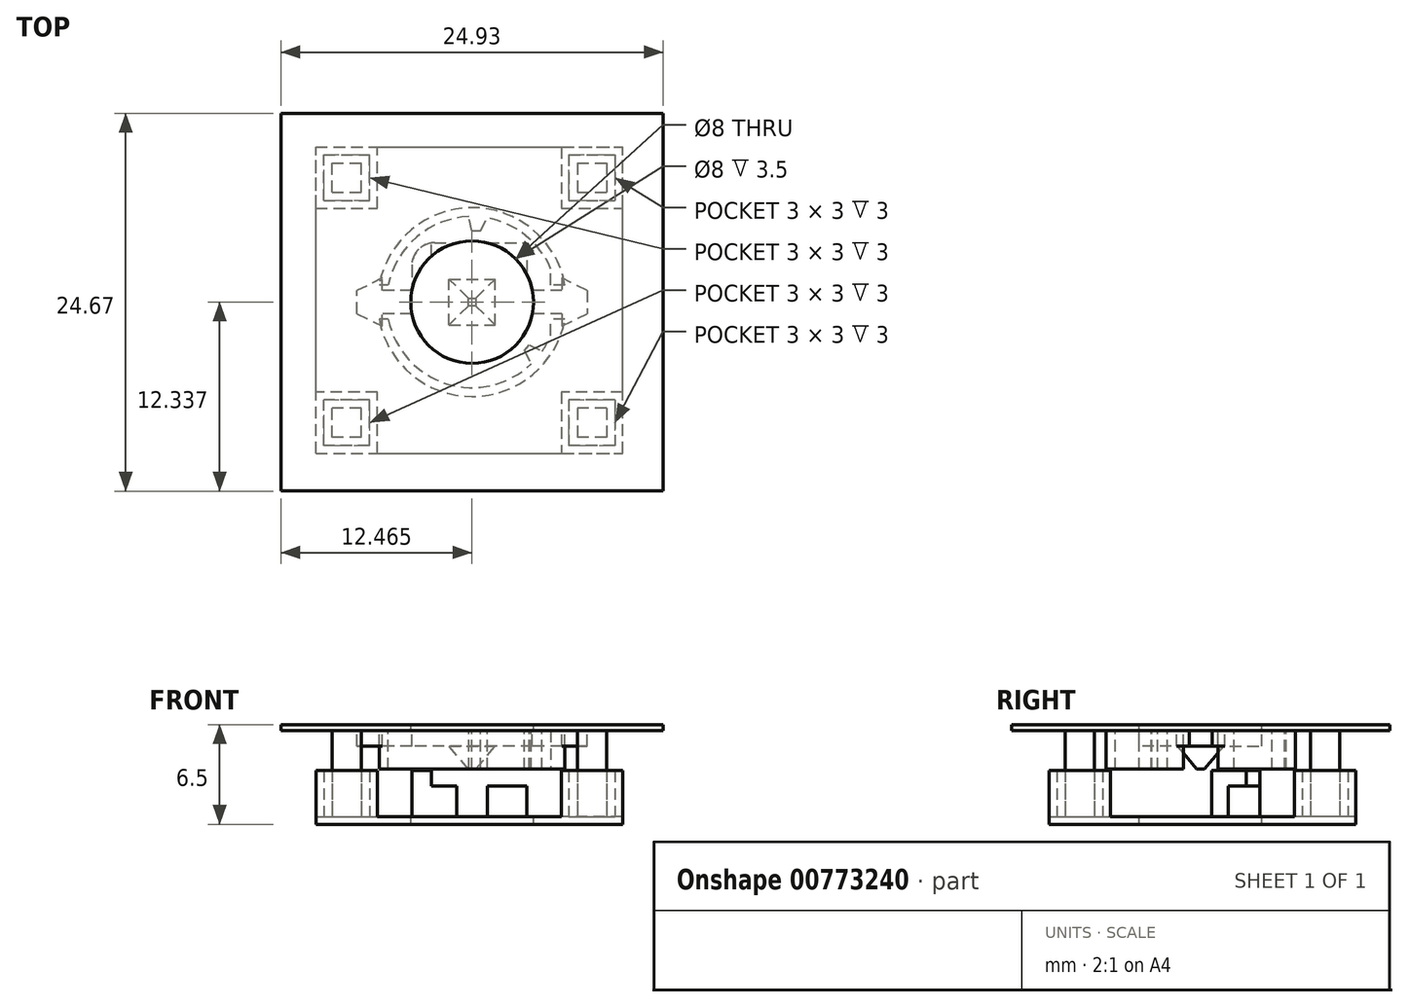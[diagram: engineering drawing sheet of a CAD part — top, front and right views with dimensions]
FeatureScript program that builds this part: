
annotation { "Feature Type Name" : "Feature", "Feature Type Description" : "" }
export const myFeature = defineFeature(function(context is Context, id is Id, definition is map)
    precondition{}
    {
        {
            var Q0;
            Q0=qCreatedBy(makeId("Top.planeOp"),FACE);
            var sketch = newSketch(context, id + "F0", { "sketchPlane" : qUnion([Q0])});
            skLineSegment(sketch, "E0.bottom", {"start": v(0, 0) * mm, "end": v(20, 0) * mm});
            skLineSegment(sketch, "E0.top", {"start": v(0, 20) * mm, "end": v(20, 20) * mm});
            skLineSegment(sketch, "E0.left", {"start": v(0, 0) * mm, "end": v(0, 20) * mm});
            skLineSegment(sketch, "E0.right", {"start": v(20, 0) * mm, "end": v(20, 20) * mm});
            skSolve(sketch);
        }
        {
            var Q0;
            Q0=makeQuery(id+"F0.imprint","IMPRINT",FACE,{"disambiguationData":[TD([[makeQuery(id+"F0.imprint","IMPRINT",EDGE,{"derivedFrom":sQuery(id+"F0.wireOp",EDGE,"E0.bottom")}),1.0]])]});
            extrude(context, id + "F1", {"entities" : qUnion([Q0]), "depth" : 0.5 * mm, "offsetDistance" : 25 * mm});
        }
        {
            var Q0;
            Q0=makeQuery(id+"F1.opExtrude","CAP_FACE",FACE,{"disambiguationData":[OSD([sQuery(id+"F0.wireOp",EDGE,"E0.bottom"),sQuery(id+"F0.wireOp",EDGE,"E0.top"),sQuery(id+"F0.wireOp",EDGE,"E0.left"),sQuery(id+"F0.wireOp",EDGE,"E0.right")])],"isStart":false});
            var sketch = newSketch(context, id + "F2", { "sketchPlane" : qUnion([Q0])});
            skLineSegment(sketch, "E1.bottom", {"start": v(16.5, 19.5) * mm, "end": v(19.5, 19.5) * mm});
            skLineSegment(sketch, "E1.top", {"start": v(16.5, 16.5) * mm, "end": v(19.5, 16.5) * mm});
            skLineSegment(sketch, "E1.left", {"start": v(16.5, 19.5) * mm, "end": v(16.5, 16.5) * mm});
            skLineSegment(sketch, "E1.right", {"start": v(19.5, 19.5) * mm, "end": v(19.5, 16.5) * mm});
            skPoint(sketch, "E2.middle.positionSnap0", {"position": v(19.5, 18) * mm});
            skPoint(sketch, "E2.middle.positionSnap1", {"position": v(18, 19.5) * mm});
            skPoint(sketch, "E2.centerSnap0", {"position": v(19.5, 18) * mm});
            skPoint(sketch, "E2.centerSnap1", {"position": v(18, 19.5) * mm});
            skLineSegment(sketch, "E3.0", {"start": v(16, 20) * mm, "end": v(20, 20) * mm});
            skLineSegment(sketch, "E3.1", {"start": v(16, 20) * mm, "end": v(16, 16) * mm});
            skLineSegment(sketch, "E3.2", {"start": v(16, 16) * mm, "end": v(20, 16) * mm});
            skLineSegment(sketch, "E3.3", {"start": v(20, 20) * mm, "end": v(20, 16) * mm});
            skLineSegment(sketch, "E4.0", {"start": v(17.05, 18.95) * mm, "end": v(18.95, 18.95) * mm});
            skLineSegment(sketch, "E4.1", {"start": v(17.05, 18.95) * mm, "end": v(17.05, 17.05) * mm});
            skLineSegment(sketch, "E4.2", {"start": v(17.05, 17.05) * mm, "end": v(18.95, 17.05) * mm});
            skLineSegment(sketch, "E4.3", {"start": v(18.95, 18.95) * mm, "end": v(18.95, 17.05) * mm});
            skLineSegment(sketch, "E5.1.0", {"start": v(0, 20) * mm, "end": v(4, 20) * mm});
            skLineSegment(sketch, "E5.1.1", {"start": v(4, 16) * mm, "end": v(4, 20) * mm});
            skLineSegment(sketch, "E5.1.2", {"start": v(0, 16) * mm, "end": v(4, 16) * mm});
            skLineSegment(sketch, "E5.1.3", {"start": v(1.05, 17.05) * mm, "end": v(2.95, 17.05) * mm});
            skLineSegment(sketch, "E5.1.4", {"start": v(3.5, 16.5) * mm, "end": v(3.5, 19.5) * mm});
            skLineSegment(sketch, "E5.1.5", {"start": v(0, 16) * mm, "end": v(0, 20) * mm});
            skLineSegment(sketch, "E5.1.6", {"start": v(2.95, 17.05) * mm, "end": v(2.95, 18.95) * mm});
            skLineSegment(sketch, "E5.1.7", {"start": v(0.5, 16.5) * mm, "end": v(3.5, 16.5) * mm});
            skPoint(sketch, "E5.1.8", {"position": v(2, 19.5) * mm});
            skLineSegment(sketch, "E5.1.9", {"start": v(1.05, 17.05) * mm, "end": v(1.05, 18.95) * mm});
            skPoint(sketch, "E5.1.10", {"position": v(0.5, 18) * mm});
            skPoint(sketch, "E5.1.11", {"position": v(2, 19.5) * mm});
            skLineSegment(sketch, "E5.1.12", {"start": v(0.5, 16.5) * mm, "end": v(0.5, 19.5) * mm});
            skPoint(sketch, "E5.1.13", {"position": v(0.5, 18) * mm});
            skLineSegment(sketch, "E5.1.14", {"start": v(1.05, 18.95) * mm, "end": v(2.95, 18.95) * mm});
            skLineSegment(sketch, "E5.1.15", {"start": v(0.5, 19.5) * mm, "end": v(3.5, 19.5) * mm});
            skLineSegment(sketch, "E5.2.0", {"start": v(0, 0) * mm, "end": v(0, 4) * mm});
            skLineSegment(sketch, "E5.2.1", {"start": v(4, 4) * mm, "end": v(0, 4) * mm});
            skLineSegment(sketch, "E5.2.2", {"start": v(4, 0) * mm, "end": v(4, 4) * mm});
            skLineSegment(sketch, "E5.2.3", {"start": v(2.95, 1.05) * mm, "end": v(2.95, 2.95) * mm});
            skLineSegment(sketch, "E5.2.4", {"start": v(3.5, 3.5) * mm, "end": v(0.5, 3.5) * mm});
            skLineSegment(sketch, "E5.2.5", {"start": v(4, 0) * mm, "end": v(0, 0) * mm});
            skLineSegment(sketch, "E5.2.6", {"start": v(2.95, 2.95) * mm, "end": v(1.05, 2.95) * mm});
            skLineSegment(sketch, "E5.2.7", {"start": v(3.5, 0.5) * mm, "end": v(3.5, 3.5) * mm});
            skPoint(sketch, "E5.2.8", {"position": v(0.5, 2) * mm});
            skLineSegment(sketch, "E5.2.9", {"start": v(2.95, 1.05) * mm, "end": v(1.05, 1.05) * mm});
            skPoint(sketch, "E5.2.10", {"position": v(2, 0.5) * mm});
            skPoint(sketch, "E5.2.11", {"position": v(0.5, 2) * mm});
            skLineSegment(sketch, "E5.2.12", {"start": v(3.5, 0.5) * mm, "end": v(0.5, 0.5) * mm});
            skPoint(sketch, "E5.2.13", {"position": v(2, 0.5) * mm});
            skLineSegment(sketch, "E5.2.14", {"start": v(1.05, 1.05) * mm, "end": v(1.05, 2.95) * mm});
            skLineSegment(sketch, "E5.2.15", {"start": v(0.5, 0.5) * mm, "end": v(0.5, 3.5) * mm});
            skLineSegment(sketch, "E5.3.0", {"start": v(20, 0) * mm, "end": v(16, 0) * mm});
            skLineSegment(sketch, "E5.3.1", {"start": v(16, 4) * mm, "end": v(16, 0) * mm});
            skLineSegment(sketch, "E5.3.2", {"start": v(20, 4) * mm, "end": v(16, 4) * mm});
            skLineSegment(sketch, "E5.3.3", {"start": v(18.95, 2.95) * mm, "end": v(17.05, 2.95) * mm});
            skLineSegment(sketch, "E5.3.4", {"start": v(16.5, 3.5) * mm, "end": v(16.5, 0.5) * mm});
            skLineSegment(sketch, "E5.3.5", {"start": v(20, 4) * mm, "end": v(20, 0) * mm});
            skLineSegment(sketch, "E5.3.6", {"start": v(17.05, 2.95) * mm, "end": v(17.05, 1.05) * mm});
            skLineSegment(sketch, "E5.3.7", {"start": v(19.5, 3.5) * mm, "end": v(16.5, 3.5) * mm});
            skPoint(sketch, "E5.3.8", {"position": v(18, 0.5) * mm});
            skLineSegment(sketch, "E5.3.9", {"start": v(18.95, 2.95) * mm, "end": v(18.95, 1.05) * mm});
            skPoint(sketch, "E5.3.10", {"position": v(19.5, 2) * mm});
            skPoint(sketch, "E5.3.11", {"position": v(18, 0.5) * mm});
            skLineSegment(sketch, "E5.3.12", {"start": v(19.5, 3.5) * mm, "end": v(19.5, 0.5) * mm});
            skPoint(sketch, "E5.3.13", {"position": v(19.5, 2) * mm});
            skLineSegment(sketch, "E5.3.14", {"start": v(18.95, 1.05) * mm, "end": v(17.05, 1.05) * mm});
            skLineSegment(sketch, "E5.3.15", {"start": v(19.5, 0.5) * mm, "end": v(16.5, 0.5) * mm});
            skPoint(sketch, "E5.center", {"position": v(10, 10) * mm});
            skSolve(sketch);
        }
        {
            var Q0;
            Q0=makeQuery(id+"F2.imprint","IMPRINT",FACE,{"disambiguationData":[TD([[makeQuery(id+"F2.imprint","IMPRINT",EDGE,{"derivedFrom":sQuery(id+"F2.wireOp",EDGE,"E1.bottom")}),1.0]])]});
            var Q1;
            Q1=makeQuery(id+"F2.imprint","IMPRINT",FACE,{"disambiguationData":[TD([[makeQuery(id+"F2.imprint","IMPRINT",EDGE,{"derivedFrom":sQuery(id+"F2.wireOp",EDGE,"E5.1.0")}),-1.0]])]});
            var Q2;
            Q2=makeQuery(id+"F2.imprint","IMPRINT",FACE,{"disambiguationData":[TD([[makeQuery(id+"F2.imprint","IMPRINT",EDGE,{"derivedFrom":sQuery(id+"F2.wireOp",EDGE,"E5.2.0")}),-1.0]])]});
            var Q3;
            Q3=makeQuery(id+"F2.imprint","IMPRINT",FACE,{"disambiguationData":[TD([[makeQuery(id+"F2.imprint","IMPRINT",EDGE,{"derivedFrom":sQuery(id+"F2.wireOp",EDGE,"E5.3.0")}),-1.0]])]});
            var Q4;
            Q4=makeQuery(id+"F2.imprint","IMPRINT",FACE,{"disambiguationData":[TD([[makeQuery(id+"F2.imprint","IMPRINT",EDGE,{"derivedFrom":sQuery(id+"F2.wireOp",EDGE,"E5.3.0")}),1.0]])]});
            extrude(context, id + "F3", {"entities" : qUnion([Q0, Q1, Q2, Q3, Q4]), "operationType" : NewBodyOperationType.ADD, "depth" : 3 * mm, "offsetDistance" : 25 * mm});
        }
        {
            var Q0;
            Q0=makeQuery(id+"F2.imprint","IMPRINT",FACE,{"disambiguationData":[TD([[makeQuery(id+"F2.imprint","IMPRINT",EDGE,{"derivedFrom":sQuery(id+"F2.wireOp",EDGE,"E5.1.3")}),1.0]])]});
            var Q1;
            Q1=makeQuery(id+"F2.imprint","IMPRINT",FACE,{"disambiguationData":[TD([[makeQuery(id+"F2.imprint","IMPRINT",EDGE,{"derivedFrom":sQuery(id+"F2.wireOp",EDGE,"E4.0")}),-1.0]])]});
            var Q2;
            Q2=makeQuery(id+"F2.imprint","IMPRINT",FACE,{"disambiguationData":[TD([[makeQuery(id+"F2.imprint","IMPRINT",EDGE,{"derivedFrom":sQuery(id+"F2.wireOp",EDGE,"E5.3.3")}),1.0]])]});
            var Q3;
            Q3=makeQuery(id+"F2.imprint","IMPRINT",FACE,{"disambiguationData":[TD([[makeQuery(id+"F2.imprint","IMPRINT",EDGE,{"derivedFrom":sQuery(id+"F2.wireOp",EDGE,"E5.2.3")}),1.0]])]});
            extrude(context, id + "F4", {"entities" : qUnion([Q0, Q1, Q2, Q3]), "depth" : 6 * mm, "offsetDistance" : 25 * mm});
        }
        {
            var Q0;
            Q0=makeQuery(id+"F4.opExtrude","CAP_FACE",FACE,{"disambiguationData":[OSD([sQuery(id+"F2.wireOp",EDGE,"E4.0"),sQuery(id+"F2.wireOp",EDGE,"E4.1"),sQuery(id+"F2.wireOp",EDGE,"E4.2"),sQuery(id+"F2.wireOp",EDGE,"E4.3")])],"isStart":false});
            var sketch = newSketch(context, id + "F5", { "sketchPlane" : qUnion([Q0])});
            skLineSegment(sketch, "E6.bottom", {"start": v(22.65, 22.21) * mm, "end": v(-2.28, 22.21) * mm});
            skLineSegment(sketch, "E6.top", {"start": v(22.65, -2.46) * mm, "end": v(-2.28, -2.46) * mm});
            skLineSegment(sketch, "E6.left", {"start": v(22.65, 22.21) * mm, "end": v(22.65, -2.46) * mm});
            skLineSegment(sketch, "E6.right", {"start": v(-2.28, 22.21) * mm, "end": v(-2.28, -2.46) * mm});
            skSolve(sketch);
        }
        {
            var Q0;
            Q0=makeQuery(id+"F5.imprint","IMPRINT",FACE,{"disambiguationData":[TD([[makeQuery(id+"F5.imprint","IMPRINT",EDGE,{"derivedFrom":sQuery(id+"F5.wireOp",EDGE,"E6.bottom")}),1.0]])]});
            extrude(context, id + "F6", {"entities" : qUnion([Q0]), "operationType" : NewBodyOperationType.ADD, "oppositeDirection" : true, "depth" : 0.4 * mm, "offsetDistance" : 25 * mm});
        }
        {
            var Q0;
            {var subQ0=sQuery(id+"F2.wireOp",EDGE,"E4.3");var subQ1=sQuery(id+"F2.wireOp",EDGE,"E4.2");var subQ2=sQuery(id+"F2.wireOp",EDGE,"E4.1");var subQ3=sQuery(id+"F2.wireOp",EDGE,"E4.0");Q0=makeQuery(id+"F6.boolean.opBoolean","MERGE",FACE,{"derivedFrom":[makeQuery(id+"F4.opExtrude","CAP_FACE",FACE,{"disambiguationData":[OSD([subQ3,subQ2,subQ1,subQ0])],"isStart":false}),makeQuery(id+"F4.opExtrude","CAP_FACE",FACE,{"disambiguationData":[OSD([sQuery(id+"F2.wireOp",EDGE,"E5.1.3"),sQuery(id+"F2.wireOp",EDGE,"E5.1.6"),sQuery(id+"F2.wireOp",EDGE,"E5.1.9"),sQuery(id+"F2.wireOp",EDGE,"E5.1.14")])],"isStart":false}),makeQuery(id+"F4.opExtrude","CAP_FACE",FACE,{"disambiguationData":[OSD([sQuery(id+"F2.wireOp",EDGE,"E5.2.3"),sQuery(id+"F2.wireOp",EDGE,"E5.2.6"),sQuery(id+"F2.wireOp",EDGE,"E5.2.9"),sQuery(id+"F2.wireOp",EDGE,"E5.2.14")])],"isStart":false}),makeQuery(id+"F4.opExtrude","CAP_FACE",FACE,{"disambiguationData":[OSD([sQuery(id+"F2.wireOp",EDGE,"E5.3.3"),sQuery(id+"F2.wireOp",EDGE,"E5.3.6"),sQuery(id+"F2.wireOp",EDGE,"E5.3.9"),sQuery(id+"F2.wireOp",EDGE,"E5.3.14")])],"isStart":false}),makeQuery(id+"F6.opExtrude","CAP_FACE",FACE,{"disambiguationData":[OSD([subQ3,subQ2,subQ1,subQ0,sQuery(id+"F5.wireOp",EDGE,"E6.bottom"),sQuery(id+"F5.wireOp",EDGE,"E6.top"),sQuery(id+"F5.wireOp",EDGE,"E6.left"),sQuery(id+"F5.wireOp",EDGE,"E6.right")])],"isStart":true})]});}
            var sketch = newSketch(context, id + "F7", { "sketchPlane" : qUnion([Q0])});
            skCircle(sketch, "E7", {"center": v(10.18, 9.88) * mm, "radius": 4 * mm});
            skPoint(sketch, "E7.centerSnap0", {"position": v(10.18, 22.21) * mm});
            skPoint(sketch, "E7.centerSnap1", {"position": v(22.65, 9.88) * mm});
            skSolve(sketch);
        }
        {
            var Q0;
            Q0=makeQuery(id+"F7.imprint","IMPRINT",FACE,{"disambiguationData":[TD([[makeQuery(id+"F7.imprint","IMPRINT",EDGE,{"derivedFrom":sQuery(id+"F7.wireOp",EDGE,"E7")}),1.0]])]});
            extrude(context, id + "F8", {"entities" : qUnion([Q0]), "operationType" : NewBodyOperationType.REMOVE, "oppositeDirection" : true, "depth" : 25 * mm, "offsetDistance" : 25 * mm});
        }
        {
            var Q0;
            Q0=makeQuery(id+"FnoxdWEcKo2KXdU_3.boolean.opBoolean","MERGE",FACE,{"derivedFrom":[makeQuery(id+"F6.opExtrude","CAP_FACE",FACE,{"disambiguationData":[OSD([sQuery(id+"F2.wireOp",EDGE,"E4.0"),sQuery(id+"F2.wireOp",EDGE,"E4.1"),sQuery(id+"F2.wireOp",EDGE,"E4.2"),sQuery(id+"F2.wireOp",EDGE,"E4.3"),sQuery(id+"F5.wireOp",EDGE,"E6.bottom"),sQuery(id+"F5.wireOp",EDGE,"E6.top"),sQuery(id+"F5.wireOp",EDGE,"E6.left"),sQuery(id+"F5.wireOp",EDGE,"E6.right")])],"isStart":false}),makeQuery(id+"FnoxdWEcKo2KXdU_3.opExtrude","SWEPT_FACE",FACE,{"disambiguationData":[OSD([sQuery(id+"F0zA4uYZW5pRUPb_3.wireOp",EDGE,"ZhX8Fjgi-kqvp-VlpE-l4Rn-IeRyZbtZChRy.bottom")])]})]});
            var sketch = newSketch(context, id + "F9", { "sketchPlane" : qUnion([Q0])});
            skLineSegment(sketch, "E8", {"start": v(10.18, -9.88) * mm, "end": v(14.18, -9.88) * mm});
            skLineSegment(sketch, "E9", {"start": v(10.18, -9.88) * mm, "end": v(13.75, -6.89) * mm});
            skLineSegment(sketch, "E10", {"start": v(13.59, -6.7) * mm, "end": v(13.9, -7.08) * mm});
            skLineSegment(sketch, "E11", {"start": v(10.18, -9.88) * mm, "end": v(10.18, -14.53) * mm});
            skLineSegment(sketch, "E12", {"start": v(10.18, -14.53) * mm, "end": v(10.75, -14.53) * mm});
            skCircle(sketch, "E13", {"center": v(10.18, -9.88) * mm, "radius": 5.58 * mm});
            skCircle(sketch, "E14", {"center": v(10.18, -9.88) * mm, "radius": 6.17 * mm});
            skLineSegment(sketch, "E15", {"start": v(10.75, -14.53) * mm, "end": v(11.17, -15.37) * mm});
            skLineSegment(sketch, "E16", {"start": v(10.18, -14.53) * mm, "end": v(9.97, -15.45) * mm});
            skLineSegment(sketch, "E17", {"start": v(13.59, -6.7) * mm, "end": v(14.05, -5.85) * mm});
            skLineSegment(sketch, "E18", {"start": v(13.9, -7.08) * mm, "end": v(14.75, -6.67) * mm});
            skLineSegment(sketch, "E19", {"start": v(15.32, -7.7) * mm, "end": v(15.32, -12.05) * mm});
            skSolve(sketch);
        }
        {
            var Q0;
            {var subQ0=sQuery(id+"F9.wireOp",EDGE,"scZHxu3C-Op0m-khkx-aFYf-Y6gfYPpbK4Jl");Q0=makeQuery(id+"F9.imprint","IMPRINT",FACE,{"disambiguationData":[TD([[makeQuery(id+"F9.imprint","IMPRINT",EDGE,{"derivedFrom":subQ0}),-1.0]])]});}
            var Q1;
            Q1=makeQuery(id+"F9.imprint","IMPRINT",FACE,{"disambiguationData":[TD([[makeQuery(id+"F9.imprint","IMPRINT",EDGE,{"derivedFrom":sQuery(id+"F9.wireOp",EDGE,"E12")}),-1.0]])]});
            var Q2;
            {var subQ5=sQuery(id+"F9.wireOp",EDGE,"F097BGmS-OGrE-Bj6g-8D74-8TD7AIuaI6WG");Q2=makeQuery(id+"F9.imprint","IMPRINT",FACE,{"disambiguationData":[TD([[makeQuery(id+"F9.imprint","IMPRINT",EDGE,{"derivedFrom":subQ5}),1.0]])]});}
            var Q3;
            {var subQ0=sQuery(id+"F9.wireOp",EDGE,"E17");Q3=makeQuery(id+"F9.imprint","IMPRINT",FACE,{"disambiguationData":[TD([[makeQuery(id+"F9.imprint","IMPRINT",EDGE,{"derivedFrom":subQ0}),-1.0]])]});}
            var Q4;
            Q4=makeQuery(id+"F9.imprint","IMPRINT",FACE,{"disambiguationData":[TD([[makeQuery(id+"F9.imprint","IMPRINT",EDGE,{"derivedFrom":sQuery(id+"F9.wireOp",EDGE,"E14")}),1.0]])]});
            var Q5;
            {var subQ0=sQuery(id+"F9.wireOp",EDGE,"E19");Q5=makeQuery(id+"F9.imprint","IMPRINT",FACE,{"disambiguationData":[TD([[makeQuery(id+"F9.imprint","IMPRINT",EDGE,{"derivedFrom":subQ0}),1.0]])]});}
            extrude(context, id + "F10", {"entities" : qUnion([Q0, Q1, Q2, Q3, Q4, Q5]), "operationType" : NewBodyOperationType.ADD, "depth" : 2.5 * mm, "offsetDistance" : 25 * mm});
        }
        {
            var Q0;
            {var subQ0=sQuery(id+"F0.wireOp",EDGE,"E0.bottom");var subQ1=sQuery(id+"F0.wireOp",EDGE,"E0.right");var subQ2=sQuery(id+"F0.wireOp",EDGE,"E0.top");var subQ3=sQuery(id+"F0.wireOp",EDGE,"E0.left");Q0=makeQuery(id+"F3.boolean.opBoolean","SPLIT",FACE,{"disambiguationData":[TD([makeQuery(id+"F1.opExtrude","SWEPT_FACE",FACE,{"disambiguationData":[OSD([subQ0])]})])],"derivedFrom":makeQuery(id+"F1.opExtrude","CAP_FACE",FACE,{"disambiguationData":[OSD([subQ0,subQ2,subQ3,subQ1])],"isStart":false})});}
            var sketch = newSketch(context, id + "F11", { "sketchPlane" : qUnion([Q0])});
            skLineSegment(sketch, "E20.bottom", {"start": v(6.25, 13.75) * mm, "end": v(13.75, 13.75) * mm});
            skLineSegment(sketch, "E20.top", {"start": v(6.25, 6.25) * mm, "end": v(13.75, 6.25) * mm});
            skLineSegment(sketch, "E20.left", {"start": v(6.25, 13.75) * mm, "end": v(6.25, 6.25) * mm});
            skLineSegment(sketch, "E20.right", {"start": v(13.75, 13.75) * mm, "end": v(13.75, 6.25) * mm});
            skPoint(sketch, "E20.middle", {"position": v(10, 10) * mm});
            skPoint(sketch, "E20.middle.positionSnap0", {"position": v(0, 10) * mm});
            skPoint(sketch, "E20.middle.positionSnap1", {"position": v(10, 0) * mm});
            skPoint(sketch, "E20.centerSnap0", {"position": v(0, 10) * mm});
            skPoint(sketch, "E20.centerSnap1", {"position": v(10, 0) * mm});
            skSolve(sketch);
        }
        {
            var Q0;
            Q0=makeQuery(id+"F11.imprint","IMPRINT",FACE,{"disambiguationData":[TD([[makeQuery(id+"F11.imprint","IMPRINT",EDGE,{"derivedFrom":sQuery(id+"F11.wireOp",EDGE,"E20.bottom")}),-1.0]])]});
            extrude(context, id + "F12", {"entities" : qUnion([Q0]), "operationType" : NewBodyOperationType.ADD, "depth" : 2 * mm, "offsetDistance" : 25 * mm});
        }
        {
            var Q0;
            Q0=makeQuery(id+"F12.opExtrude","CAP_FACE",FACE,{"disambiguationData":[OSD([sQuery(id+"F11.wireOp",EDGE,"E20.bottom"),sQuery(id+"F11.wireOp",EDGE,"E20.top"),sQuery(id+"F11.wireOp",EDGE,"E20.left"),sQuery(id+"F11.wireOp",EDGE,"E20.right")])],"isStart":false});
            var sketch = newSketch(context, id + "F13", { "sketchPlane" : qUnion([Q0])});
            skLineSegment(sketch, "E21", {"start": v(12.47, 6.25) * mm, "end": v(12.47, 13.75) * mm});
            skLineSegment(sketch, "E22", {"start": v(7.52, 6.25) * mm, "end": v(7.52, 13.75) * mm});
            skLineSegment(sketch, "E23", {"start": v(7.52, 10) * mm, "end": v(6.25, 10) * mm, "construction": true});
            skLineSegment(sketch, "E24", {"start": v(12.47, 10) * mm, "end": v(13.75, 10) * mm, "construction": true});
            skLineSegment(sketch, "E25", {"start": v(12.47, 7.13) * mm, "end": v(7.52, 7.13) * mm});
            skSolve(sketch);
        }
        {
            var Q0;
            {var subQ0=makeQuery(id+"F12.opExtrude","CAP_EDGE",EDGE,{"disambiguationData":[OSD([sQuery(id+"F11.wireOp",EDGE,"E20.right")])],"isStart":false});Q0=makeQuery(id+"F13.imprint","IMPRINT",FACE,{"disambiguationData":[TD([[makeQuery(id+"F13.imprint","IMPRINT",EDGE,{"derivedFrom":subQ0}),-1.0]])]});}
            var Q1;
            {var subQ3=sQuery(id+"F13.wireOp",EDGE,"E25");Q1=makeQuery(id+"F13.imprint","IMPRINT",FACE,{"disambiguationData":[TD([[makeQuery(id+"F13.imprint","IMPRINT",EDGE,{"derivedFrom":subQ3}),1.0]])]});}
            var Q2;
            {var subQ0=makeQuery(id+"F12.opExtrude","CAP_EDGE",EDGE,{"disambiguationData":[OSD([sQuery(id+"F11.wireOp",EDGE,"E20.left")])],"isStart":false});Q2=makeQuery(id+"F13.imprint","IMPRINT",FACE,{"disambiguationData":[TD([[makeQuery(id+"F13.imprint","IMPRINT",EDGE,{"derivedFrom":subQ0}),1.0]])]});}
            extrude(context, id + "F14", {"entities" : qUnion([Q0, Q1, Q2]), "operationType" : NewBodyOperationType.ADD, "depth" : 1 * mm, "offsetDistance" : 25 * mm});
        }
        {
            var Q0;
            {var subQ0=sQuery(id+"F11.wireOp",EDGE,"E20.left");var subQ1=sQuery(id+"F11.wireOp",EDGE,"E20.bottom");Q0=makeQuery(id+"F14.boolean.opBoolean","MERGE",EDGE,{"derivedFrom":[makeQuery(id+"F12.opExtrude","SWEPT_EDGE",EDGE,{"disambiguationData":[OSD([subQ1,subQ0])]}),makeQuery(id+"F14.opExtrude","SWEPT_EDGE",EDGE,{"disambiguationData":[OSD([subQ1,subQ0])]})]});}
            var Q1;
            {var subQ0=sQuery(id+"F11.wireOp",EDGE,"E20.right");var subQ1=sQuery(id+"F11.wireOp",EDGE,"E20.bottom");Q1=makeQuery(id+"F14.boolean.opBoolean","MERGE",EDGE,{"derivedFrom":[makeQuery(id+"F12.opExtrude","SWEPT_EDGE",EDGE,{"disambiguationData":[OSD([subQ1,subQ0])]}),makeQuery(id+"F14.opExtrude","SWEPT_EDGE",EDGE,{"disambiguationData":[OSD([subQ1,subQ0])]})]});}
            var Q2;
            {var subQ0=sQuery(id+"F11.wireOp",EDGE,"E20.right");var subQ1=sQuery(id+"F11.wireOp",EDGE,"E20.top");Q2=makeQuery(id+"F14.boolean.opBoolean","MERGE",EDGE,{"derivedFrom":[makeQuery(id+"F12.opExtrude","SWEPT_EDGE",EDGE,{"disambiguationData":[OSD([subQ1,subQ0])]}),makeQuery(id+"F14.opExtrude","SWEPT_EDGE",EDGE,{"disambiguationData":[OSD([subQ1,subQ0])]})]});}
            var Q3;
            {var subQ0=sQuery(id+"F11.wireOp",EDGE,"E20.left");var subQ1=sQuery(id+"F11.wireOp",EDGE,"E20.top");Q3=makeQuery(id+"F14.boolean.opBoolean","MERGE",EDGE,{"derivedFrom":[makeQuery(id+"F12.opExtrude","SWEPT_EDGE",EDGE,{"disambiguationData":[OSD([subQ1,subQ0])]}),makeQuery(id+"F14.opExtrude","SWEPT_EDGE",EDGE,{"disambiguationData":[OSD([subQ1,subQ0])]})]});}
            fillet(context, id + "F15", {"entities" : qUnion([Q0, Q1, Q2, Q3]), "radius" : 1.5 * mm, "tangentPropagation" : true, "allowEdgeOverflow" : false});
        }
        {
            var Q0;
            Q0=makeQuery(id+"F10.opExtrude","CAP_FACE",FACE,{"disambiguationData":[OSD([sQuery(id+"F9.wireOp",EDGE,"E10"),sQuery(id+"F9.wireOp",EDGE,"E12"),sQuery(id+"F9.wireOp",EDGE,"E13"),sQuery(id+"F9.wireOp",EDGE,"E14"),sQuery(id+"F9.wireOp",EDGE,"E15"),sQuery(id+"F9.wireOp",EDGE,"E16"),sQuery(id+"F9.wireOp",EDGE,"E17"),sQuery(id+"F9.wireOp",EDGE,"E18")])],"isStart":false});
            var sketch = newSketch(context, id + "F16", { "sketchPlane" : qUnion([Q0])});
            skLineSegment(sketch, "E26.bottom", {"start": v(17.68, -8.75) * mm, "end": v(2.68, -8.75) * mm});
            skLineSegment(sketch, "E26.top", {"start": v(17.68, -11) * mm, "end": v(2.68, -11) * mm});
            skLineSegment(sketch, "E26.left", {"start": v(17.68, -8.75) * mm, "end": v(17.68, -11) * mm});
            skLineSegment(sketch, "E26.right", {"start": v(2.68, -8.75) * mm, "end": v(2.68, -11) * mm});
            skPoint(sketch, "E26.middle", {"position": v(10.18, -9.88) * mm});
            skSolve(sketch);
        }
        {
            var Q0;
            Q0 = qSketchRegion(id + "F16", true);
            var Q1;
            {var subQ0=sQuery(id+"F5.wireOp",EDGE,"E6.right");var subQ1=sQuery(id+"F2.wireOp",EDGE,"E4.0");var subQ2=sQuery(id+"F2.wireOp",EDGE,"E4.3");var subQ3=sQuery(id+"F2.wireOp",EDGE,"E4.1");var subQ4=sQuery(id+"F2.wireOp",EDGE,"E4.2");var subQ5=sQuery(id+"F5.wireOp",EDGE,"E6.bottom");var subQ6=sQuery(id+"F5.wireOp",EDGE,"E6.top");var subQ7=sQuery(id+"F5.wireOp",EDGE,"E6.left");Q1=makeQuery(id+"F10.boolean.opBoolean","SPLIT",FACE,{"disambiguationData":[TD([makeQuery(id+"F4.opExtrude","SWEPT_FACE",FACE,{"disambiguationData":[OSD([subQ1])]})])],"derivedFrom":makeQuery(id+"F6.opExtrude","CAP_FACE",FACE,{"disambiguationData":[OSD([subQ1,subQ3,subQ4,subQ2,subQ5,subQ6,subQ7,subQ0])],"isStart":false})});}
            extrude(context, id + "F17", {"entities" : qUnion([Q0]), "operationType" : NewBodyOperationType.REMOVE, "endBound" : BoundingType.UP_TO_SURFACE, "oppositeDirection" : true, "depth" : 25 * mm, "endBoundEntityFace" : qUnion([Q1]), "offsetDistance" : 25 * mm});
        }
        {
            var Q0;
            {var subQ5=sQuery(id+"F5.wireOp",EDGE,"E6.right");var subQ6=sQuery(id+"F5.wireOp",EDGE,"E6.left");var subQ7=sQuery(id+"F5.wireOp",EDGE,"E6.top");var subQ8=sQuery(id+"F5.wireOp",EDGE,"E6.bottom");var subQ9=sQuery(id+"F2.wireOp",EDGE,"E4.3");var subQ10=sQuery(id+"F2.wireOp",EDGE,"E4.2");var subQ11=sQuery(id+"F2.wireOp",EDGE,"E4.1");var subQ12=sQuery(id+"F2.wireOp",EDGE,"E4.0");var subQ13=makeQuery(id+"F6.opExtrude","CAP_FACE",FACE,{"disambiguationData":[OSD([subQ12,subQ11,subQ10,subQ9,subQ8,subQ7,subQ6,subQ5])],"isStart":false});Q0=makeQuery(id+"F17.boolean.opBoolean","MERGE",FACE,{"derivedFrom":[makeQuery(id+"F10.boolean.opBoolean","SPLIT",FACE,{"disambiguationData":[TD([makeQuery(id+"F4.opExtrude","SWEPT_FACE",FACE,{"disambiguationData":[OSD([subQ12])]})])],"derivedFrom":subQ13}),makeQuery(id+"F10.boolean.opBoolean","SPLIT",FACE,{"disambiguationData":[TD([makeQuery(id+"F8.boolean.opBoolean","COPY",FACE,{"derivedFrom":makeQuery(id+"F8.opExtrude","SWEPT_FACE",FACE,{"disambiguationData":[OSD([sQuery(id+"F7.wireOp",EDGE,"E7")])]})})])],"derivedFrom":subQ13}),makeQuery(id+"F17.opExtrude","CAP_FACE",FACE,{"disambiguationData":[OSD([sQuery(id+"F16.wireOp",EDGE,"E26.bottom"),sQuery(id+"F16.wireOp",EDGE,"E26.top"),sQuery(id+"F16.wireOp",EDGE,"E26.left"),sQuery(id+"F16.wireOp",EDGE,"E26.right")])],"isStart":false})]});}
            var sketch = newSketch(context, id + "F18", { "sketchPlane" : qUnion([Q0])});
            skCircle(sketch, "E27", {"center": v(10.18, -9.88) * mm, "radius": 4 * mm});
            skLineSegment(sketch, "E28", {"start": v(10.18, -9.88) * mm, "end": v(2.68, -9.88) * mm});
            skLineSegment(sketch, "E29", {"start": v(10.18, -9.88) * mm, "end": v(17.68, -9.88) * mm});
            skLineSegment(sketch, "E30", {"start": v(17.68, -9.88) * mm, "end": v(17.68, -9.13) * mm});
            skLineSegment(sketch, "E31", {"start": v(17.68, -9.88) * mm, "end": v(17.68, -10.63) * mm});
            skLineSegment(sketch, "E32", {"start": v(2.68, -9.88) * mm, "end": v(2.68, -10.63) * mm});
            skLineSegment(sketch, "E33", {"start": v(2.68, -9.88) * mm, "end": v(2.68, -9.13) * mm});
            skLineSegment(sketch, "E34", {"start": v(17.68, -10.63) * mm, "end": v(2.68, -10.63) * mm});
            skLineSegment(sketch, "E35", {"start": v(17.68, -9.13) * mm, "end": v(2.68, -9.13) * mm});
            skLineSegment(sketch, "E36", {"start": v(2.68, -9.13) * mm, "end": v(4.32, -8.3) * mm});
            skLineSegment(sketch, "E37", {"start": v(4.32, -8.3) * mm, "end": v(4.32, -11.45) * mm});
            skLineSegment(sketch, "E38", {"start": v(4.32, -11.45) * mm, "end": v(2.68, -10.63) * mm});
            skLineSegment(sketch, "E39", {"start": v(17.68, -10.63) * mm, "end": v(16.05, -11.45) * mm});
            skLineSegment(sketch, "E40", {"start": v(16.05, -11.45) * mm, "end": v(16.05, -8.3) * mm});
            skLineSegment(sketch, "E41", {"start": v(16.05, -8.3) * mm, "end": v(17.68, -9.13) * mm});
            skSolve(sketch);
        }
        {
            var Q0;
            Q0 = qSketchRegion(id + "F18", true);
            extrude(context, id + "F19", {"entities" : qUnion([Q0]), "depth" : 1 * mm, "offsetDistance" : 25 * mm});
        }
        {
            var Q0;
            Q0=makeQuery(id+"F19.opExtrude","CAP_FACE",FACE,{"disambiguationData":[OSD([sQuery(id+"F18.wireOp",EDGE,"E27"),sQuery(id+"F18.wireOp",EDGE,"E30"),sQuery(id+"F18.wireOp",EDGE,"E31"),sQuery(id+"F18.wireOp",EDGE,"E32"),sQuery(id+"F18.wireOp",EDGE,"E33"),sQuery(id+"F18.wireOp",EDGE,"E34"),sQuery(id+"F18.wireOp",EDGE,"E35")])],"isStart":false});
            var sketch = newSketch(context, id + "F20", { "sketchPlane" : qUnion([Q0])});
            skLineSegment(sketch, "E42.bottom", {"start": v(8.68, -8.38) * mm, "end": v(11.68, -8.38) * mm});
            skLineSegment(sketch, "E42.top", {"start": v(8.68, -11.38) * mm, "end": v(11.68, -11.38) * mm});
            skLineSegment(sketch, "E42.left", {"start": v(8.68, -8.38) * mm, "end": v(8.68, -11.38) * mm});
            skLineSegment(sketch, "E42.right", {"start": v(11.68, -8.38) * mm, "end": v(11.68, -11.38) * mm});
            skPoint(sketch, "E42.middle", {"position": v(10.18, -9.88) * mm});
            skSolve(sketch);
        }
        {
            var Q0;
            Q0=makeQuery(id+"F20.imprint","IMPRINT",FACE,{"disambiguationData":[TD([[makeQuery(id+"F20.imprint","IMPRINT",EDGE,{"derivedFrom":sQuery(id+"F20.wireOp",EDGE,"E42.bottom")}),-1.0]])]});
            extrude(context, id + "F21", {"entities" : qUnion([Q0]), "operationType" : NewBodyOperationType.ADD, "depth" : 1.5 * mm, "offsetDistance" : 25 * mm});
        }
        {
            var Q0;
            Q0=makeQuery(id+"F21.opExtrude","CAP_FACE",FACE,{"disambiguationData":[OSD([sQuery(id+"F20.wireOp",EDGE,"E42.bottom"),sQuery(id+"F20.wireOp",EDGE,"E42.top"),sQuery(id+"F20.wireOp",EDGE,"E42.left"),sQuery(id+"F20.wireOp",EDGE,"E42.right")])],"isStart":false});
            chamfer(context, id + "F22", {"entities" : qUnion([Q0]), "chamferType" : ChamferType.TWO_OFFSETS, "width1" : 1.5 * mm, "oppositeDirection" : false, "width2" : 1.25 * mm, "tangentPropagation" : true});
        }
    });
